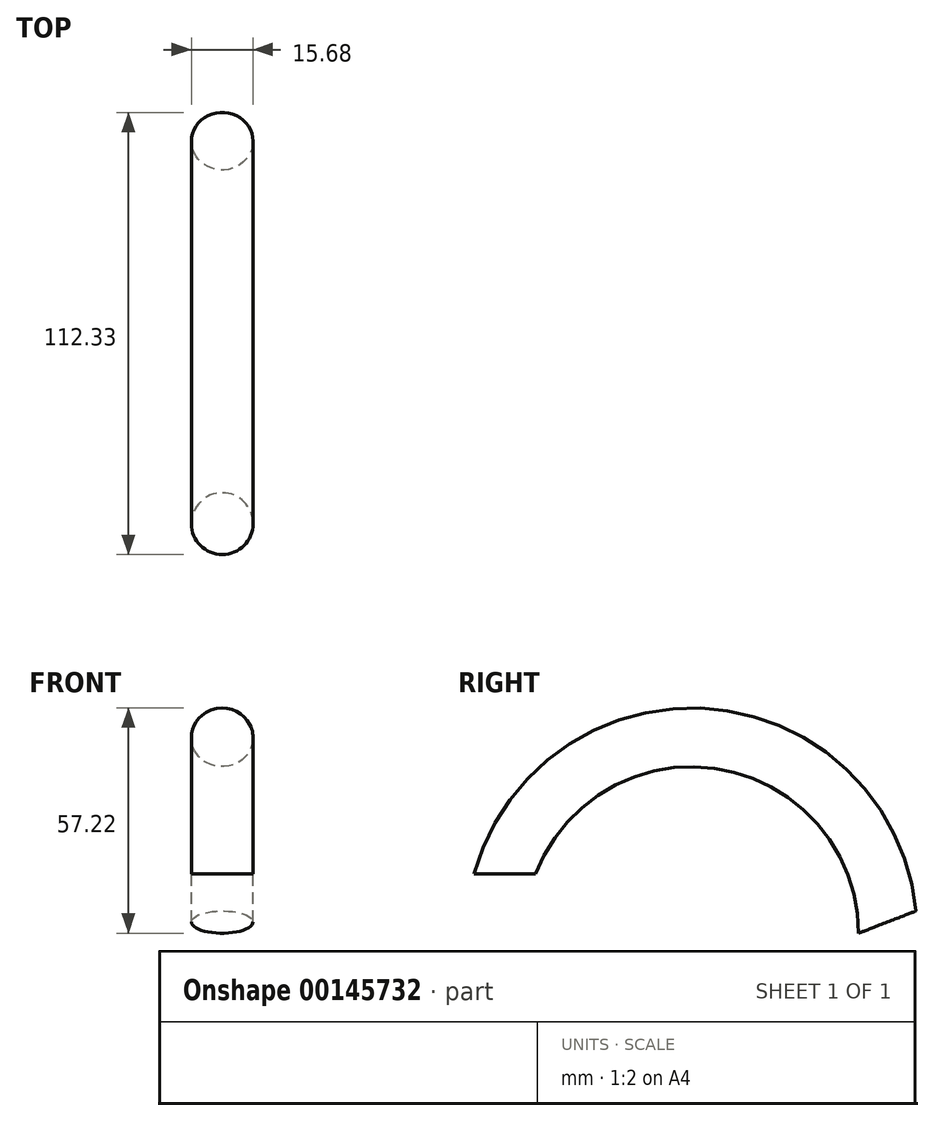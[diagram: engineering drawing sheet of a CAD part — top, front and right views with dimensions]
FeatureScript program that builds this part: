
annotation { "Feature Type Name" : "Feature", "Feature Type Description" : "" }
export const myFeature = defineFeature(function(context is Context, id is Id, definition is map)
    precondition{}
    {
        {
            var Q0;
            Q0=qCreatedBy(makeId("Top.planeOp"),FACE);
            var sketch = newSketch(context, id + "F0", { "sketchPlane" : qUnion([Q0])});
            skCircle(sketch, "E0", {"center": v(0, 51.6) * mm, "radius": 7.84 * mm});
            skSolve(sketch);
        }
        {
            var Q0;
            Q0=qCreatedBy(makeId("Right.planeOp"),FACE);
            var sketch = newSketch(context, id + "F1", { "sketchPlane" : qUnion([Q0])});
            skArc(sketch, "E1", {"start": v(148.77, -12.26) * mm, "mid": v(105.3, 34.22) * mm, "end": v(51.62, 0) * mm});
            skSolve(sketch);
        }
        {
            var Q0;
            Q0=makeQuery(id+"F0.imprint","IMPRINT",FACE,{"disambiguationData":[TD([[makeQuery(id+"F0.imprint","IMPRINT",EDGE,{"derivedFrom":sQuery(id+"F0.wireOp",EDGE,"E0")}),1.0]])]});
            var Q1;
            Q1=sQuery(id+"F1.wireOp",EDGE,"E1");
            sweep(context, id + "F2", {"profiles" : qUnion([Q0]), "path" : qUnion([Q1])});
        }
    });
